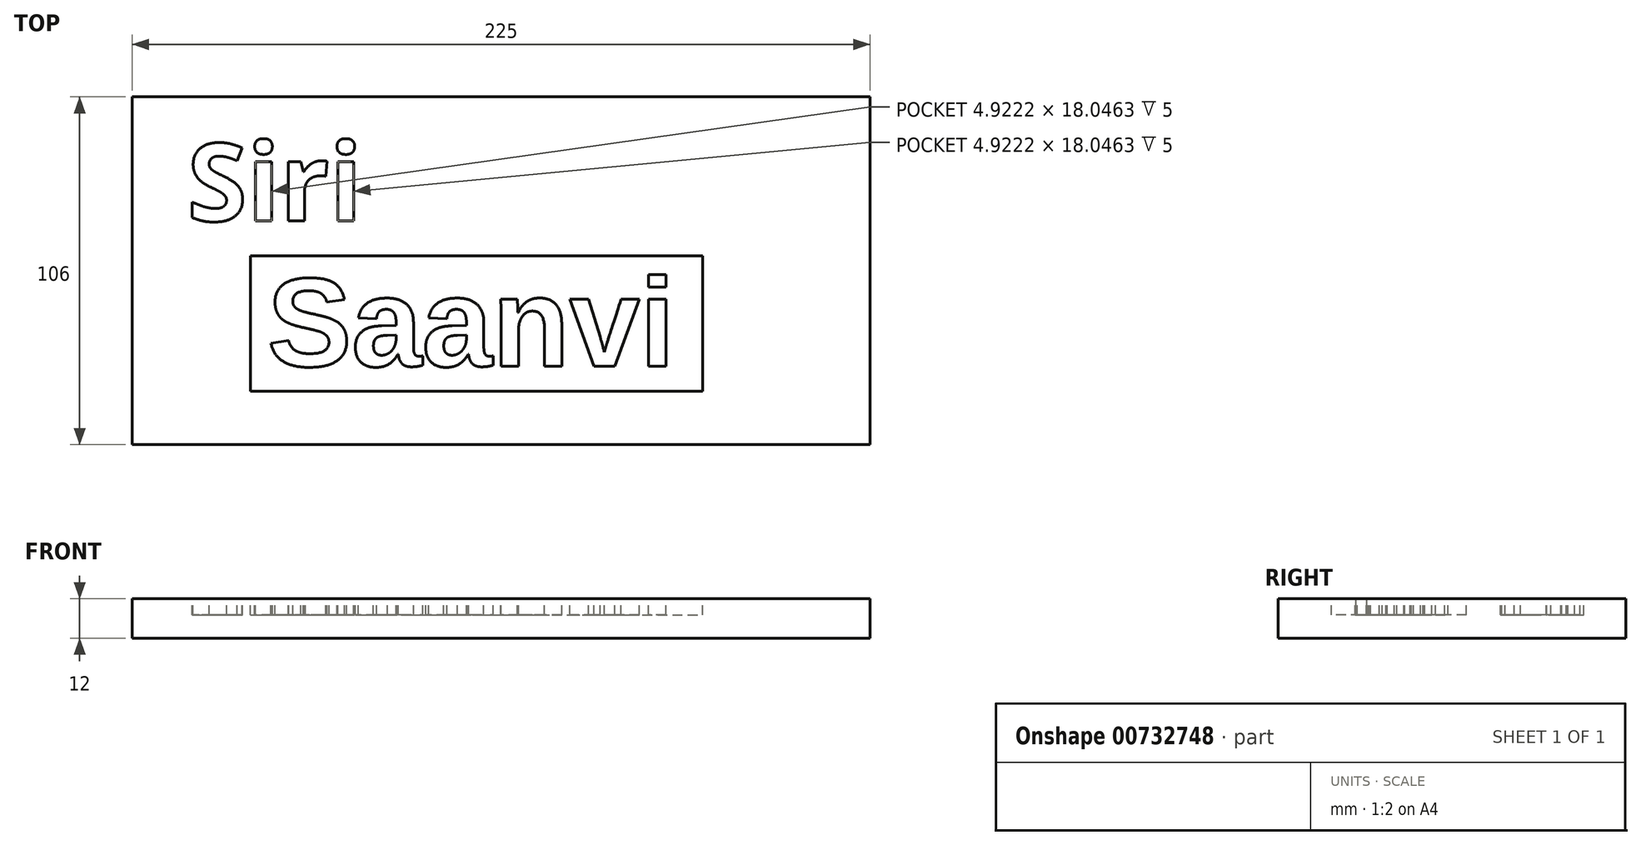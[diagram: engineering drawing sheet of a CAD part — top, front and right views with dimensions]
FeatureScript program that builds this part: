
annotation { "Feature Type Name" : "Feature", "Feature Type Description" : "" }
export const myFeature = defineFeature(function(context is Context, id is Id, definition is map)
    precondition{}
    {
        {
            var Q0;
            Q0=qCreatedBy(makeId("Top.planeOp"),FACE);
            var sketch = newSketch(context, id + "F0", { "sketchPlane" : qUnion([Q0])});
            skLineSegment(sketch, "E0.bottom", {"start": v(-167.75, 78.33) * mm, "end": v(57.25, 78.33) * mm});
            skLineSegment(sketch, "E0.top", {"start": v(-167.75, -27.67) * mm, "end": v(57.25, -27.67) * mm});
            skLineSegment(sketch, "E0.left", {"start": v(-167.75, 78.33) * mm, "end": v(-167.75, -27.67) * mm});
            skLineSegment(sketch, "E0.right", {"start": v(57.25, 78.33) * mm, "end": v(57.25, -27.67) * mm});
            skSolve(sketch);
        }
        {
            var Q0;
            Q0=makeQuery(id+"F0.imprint","IMPRINT",FACE,{"disambiguationData":[TD([[makeQuery(id+"F0.imprint","IMPRINT",EDGE,{"derivedFrom":sQuery(id+"F0.wireOp",EDGE,"E0.bottom")}),-1.0]])]});
            extrude(context, id + "F1", {"entities" : qUnion([Q0]), "depth" : 12 * mm, "offsetDistance" : 25 * mm});
        }
        {
            var Q0;
            Q0=makeQuery(id+"F1.opExtrude","CAP_FACE",FACE,{"disambiguationData":[OSD([sQuery(id+"F0.wireOp",EDGE,"E0.bottom"),sQuery(id+"F0.wireOp",EDGE,"E0.top"),sQuery(id+"F0.wireOp",EDGE,"E0.left"),sQuery(id+"F0.wireOp",EDGE,"E0.right")])],"isStart":false});
            var sketch = newSketch(context, id + "F2", { "sketchPlane" : qUnion([Q0])});
            skText(sketch, "E1", { "text": "Siri", "fontName": "OpenSans-Bold.ttf"});
            const initialGuessF2  = {"E1": [-0.15097, 0.04048, 1, 0, 0.0238]};
            skSetInitialGuess(sketch, initialGuessF2);
            skSolve(sketch);
        }
        {
            var Q0;
            Q0 = qSketchRegion(id + "F2", true);
            extrude(context, id + "F3", {"entities" : qUnion([Q0]), "operationType" : NewBodyOperationType.REMOVE, "oppositeDirection" : true, "depth" : 5 * mm, "offsetDistance" : 25 * mm});
        }
        {
            var Q0;
            Q0=makeQuery(id+"F1.opExtrude","CAP_FACE",FACE,{"disambiguationData":[OSD([sQuery(id+"F0.wireOp",EDGE,"E0.bottom"),sQuery(id+"F0.wireOp",EDGE,"E0.top"),sQuery(id+"F0.wireOp",EDGE,"E0.left"),sQuery(id+"F0.wireOp",EDGE,"E0.right")])],"isStart":false});
            var sketch = newSketch(context, id + "F4", { "sketchPlane" : qUnion([Q0])});
            skText(sketch, "E2", { "text": "Saanvi", "fontName": "Arimo-Bold.ttf"});
            skLineSegment(sketch, "E3.bottom", {"start": v(-131.75, 29.8) * mm, "end": v(6.19, 29.8) * mm});
            skLineSegment(sketch, "E3.top", {"start": v(-131.75, -11.4) * mm, "end": v(6.19, -11.4) * mm});
            skLineSegment(sketch, "E3.left", {"start": v(-131.75, 29.8) * mm, "end": v(-131.75, -11.4) * mm});
            skLineSegment(sketch, "E3.right", {"start": v(6.19, 29.8) * mm, "end": v(6.19, -11.4) * mm});
            const initialGuessF4  = {"E2": [-0.12656, -0.00377, 1, 0, 0.02777]};
            skSetInitialGuess(sketch, initialGuessF4);
            skSolve(sketch);
        }
        {
            var Q0;
            Q0=makeQuery(id+"F4.imprint","IMPRINT",FACE,{"disambiguationData":[TD([[makeQuery(id+"F4.imprint","IMPRINT",EDGE,{"derivedFrom":sQuery(id+"F4.wireOp",EDGE,"E2.sketch_text.stroke-0")}),1.0]])]});
            var Q1;
            Q1=makeQuery(id+"F4.imprint","IMPRINT",FACE,{"disambiguationData":[TD([[makeQuery(id+"F4.imprint","IMPRINT",EDGE,{"derivedFrom":sQuery(id+"F4.wireOp",EDGE,"E2.sketch_text.stroke-59")}),1.0]])]});
            var Q2;
            Q2=makeQuery(id+"F4.imprint","IMPRINT",FACE,{"disambiguationData":[TD([[makeQuery(id+"F4.imprint","IMPRINT",EDGE,{"derivedFrom":sQuery(id+"F4.wireOp",EDGE,"E2.sketch_text.stroke-97")}),1.0]])]});
            extrude(context, id + "F5", {"entities" : qUnion([Q0, Q1, Q2]), "operationType" : NewBodyOperationType.REMOVE, "oppositeDirection" : true, "depth" : 5 * mm, "offsetDistance" : 25 * mm});
        }
    });
